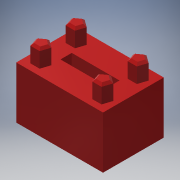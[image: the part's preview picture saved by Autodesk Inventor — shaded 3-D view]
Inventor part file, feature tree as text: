
AUTODESK INVENTOR PART (.ipt)
format: ipt  version: 2018.3 (Build 223284000, 284)  size: 224,256 bytes
history: native  units: mm
features: extrude x4, sketch x3, chamfer x2
ambient origin geometry x8: Origin, YZ Plane, XZ Plane, XY Plane, X Axis, Y Axis, Z Axis, Center Point
bodies: Solid1 (feature_tree)
feature tree (9):
  extrude  "Extrusion1"  Depth=14.0mm
  extrude  "Extrusion2"  Depth=12.0mm
  chamfer  "Chamfer1"  Distance=2.15mm
  extrude  "Extrusion3"  Depth=4.5mm
  chamfer  "Chamfer2"  Distance=4.0mm
  extrude  "Extrusion5"  Depth=4.5mm TaperAngle=45.0deg
  sketch  "Sketch1"  dims[d0=20.0mm d1=14.0mm]
  sketch  "Sketch3"  dims[d2=12.0mm d3=0.0mm d14=2.15mm d16=2.15mm d17=2.93mm]
  sketch  "Sketch5"  dims[d18=2.87mm d20=2.93mm d25=4.0mm d26=0.0mm d27=0.5mm d28=2.0mm d29=45.0deg d30=2.4mm d31=2.4mm d32=2.4mm d33=2.4mm d34=2.87mm d35=2.87mm d36=2.93mm d37=2.93mm d38=4.5mm d39=0.0mm d40=0.5mm d41=2.0mm d42=45.0deg d55=2.15mm d56=2.15mm d60=11.0mm d61=2.6mm d62=5.7mm d63=4.5mm d64=10.0mm d65=0.0mm]
